# Revit family: Haworth_Very_Chair_Seminar4Leg_Visitor_EU_PRELIMINARY
name_source: partatom
category: Furniture
revit_build: Autodesk Revit 2018 (Build: 20170223_1515(x64)
units: mm (PartAtom-declared; Revit-internal decimal feet)

## family parameters
Always vertical = Yes
Cut with Voids When Loaded = No
OmniClass Number = 23.40.70.14.64.21
OmniClass Title = Systems Furniture
Room Calculation Point = No
Shared = No
Work Plane-Based = No

## types (6) — shared parameters
Actual Depth = 56 cm
Actual Height = 86 cm
Actual Width = 60 cm
Assembly Code = E2020200
Back Finish = Haworth _ Polymer _ Glacier
Chair Finish = Haworth _ Polymer _ Glacier
Cushion Finish = Haworth _ Fabric _ Tellure _ Sky 3A-32
Description = Haworth - Very - Chair - Seminar - Visitor
Frame Finish = Haworth _ Metal _ Chrome
Glide Finish = Haworth _ Polymer _ Slate
Manufacturer = Haworth
Model = 6220
Rack Finish = Haworth _ Polymer _ Undecided
Revision Number = 3
Size = Verify Final Dim. w/ Haworth
Sustainability Info = https://www.haworth.com
Tablet Bracket Finish = Haworth _ Paint _ Black
Tablet Edge Finish = Haworth _ Laminate _ Linen H-WL
Tablet Finish = Haworth _ Laminate _ Linen H-WL
URL = https://www.haworth.com
URL - Product = https://www.haworth.com
Warranty = http://www.haworth.com

## per-type parameters (varying)
| type | Arms Actual | Tablet | With Arms | With Back Cushion | With Seat Cushion |
| No Arms - with Rack | No | No | No | No | No |
| Arms - with Rack | Yes | No | Yes | Yes | Yes |
| Tablet - with Rack | No | Yes | No | Yes | Yes |
| Arms - without Rack | Yes | No | Yes | No | No |
| No Arms - without Rack | No | No | No | No | No |
| Tablet - without Rack | No | Yes | No | No | No |

## geometry (parser evidence)
native form markers: Blend x12, Sweep x11
no freeform markers — native parametric forms only
